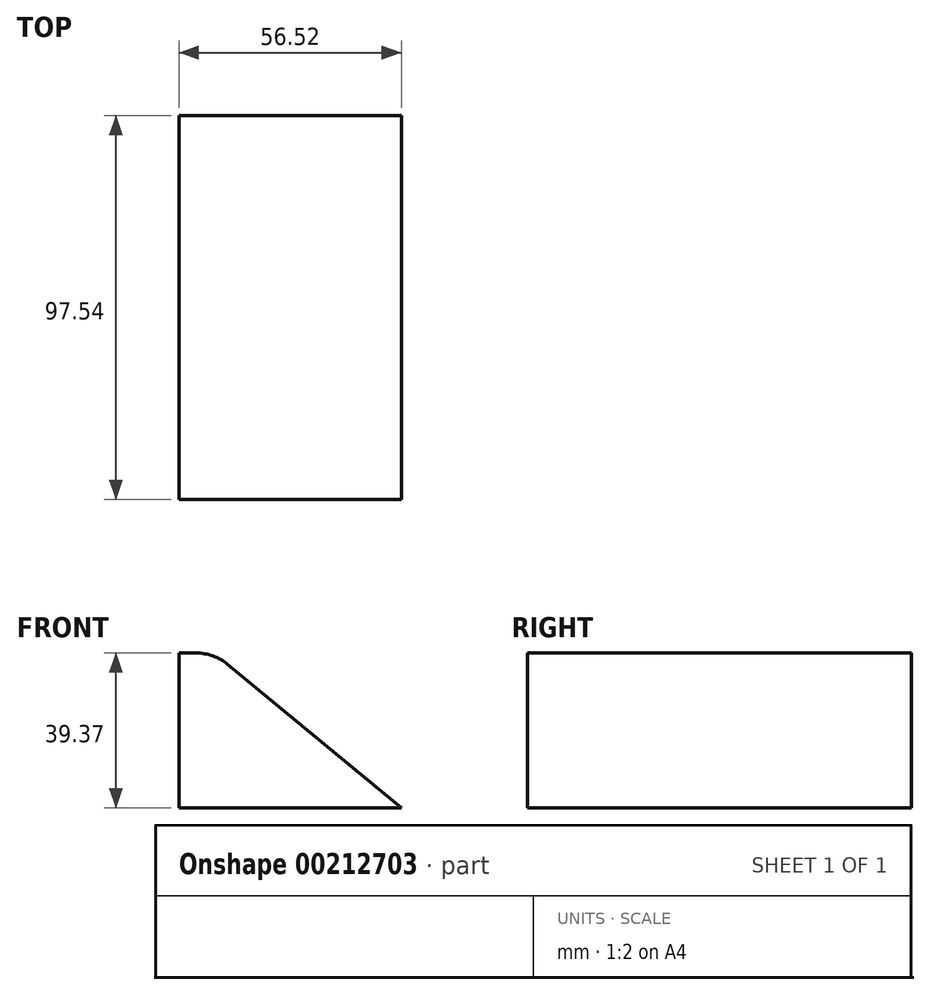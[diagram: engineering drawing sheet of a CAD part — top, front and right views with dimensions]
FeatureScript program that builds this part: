
annotation { "Feature Type Name" : "Feature", "Feature Type Description" : "" }
export const myFeature = defineFeature(function(context is Context, id is Id, definition is map)
    precondition{}
    {
        {
            var Q0;
            Q0=qCreatedBy(makeId("Front.planeOp"),FACE);
            var sketch = newSketch(context, id + "F0", { "sketchPlane" : qUnion([Q0])});
            skLineSegment(sketch, "E0", {"start": v(-54.93, 20.38) * mm, "end": v(-54.93, -19) * mm});
            skLineSegment(sketch, "E1", {"start": v(-56.26, 20.38) * mm, "end": v(-54.93, 20.38) * mm});
            skLineSegment(sketch, "E2", {"start": v(-54.93, -19) * mm, "end": v(1.59, -19) * mm});
            skLineSegment(sketch, "E3", {"start": v(-54.93, 20.38) * mm, "end": v(-50.6, 20.38) * mm});
            skLineSegment(sketch, "E4", {"start": v(-42.52, 17.47) * mm, "end": v(1.59, -19) * mm});
            skPoint(sketch, "E5.visualSharp", {"position": v(-46.04, 20.38) * mm});
            skArc(sketch, "E5.filletArc", {"start": v(-42.52, 17.47) * mm, "mid": v(-46.3, 19.63) * mm, "end": v(-50.6, 20.38) * mm});
            skLineSegment(sketch, "E6", {"start": v(1.59, -19) * mm, "end": v(63.73, 56.18) * mm});
            skSolve(sketch);
        }
        {
            var Q0;
            Q0 = qSketchRegion(id + "F0", true);
            extrude(context, id + "F1", {"entities" : qUnion([Q0]), "endBound" : BoundingType.SYMMETRIC, "oppositeDirection" : true, "depth" : 97.54 * mm});
        }
    });
